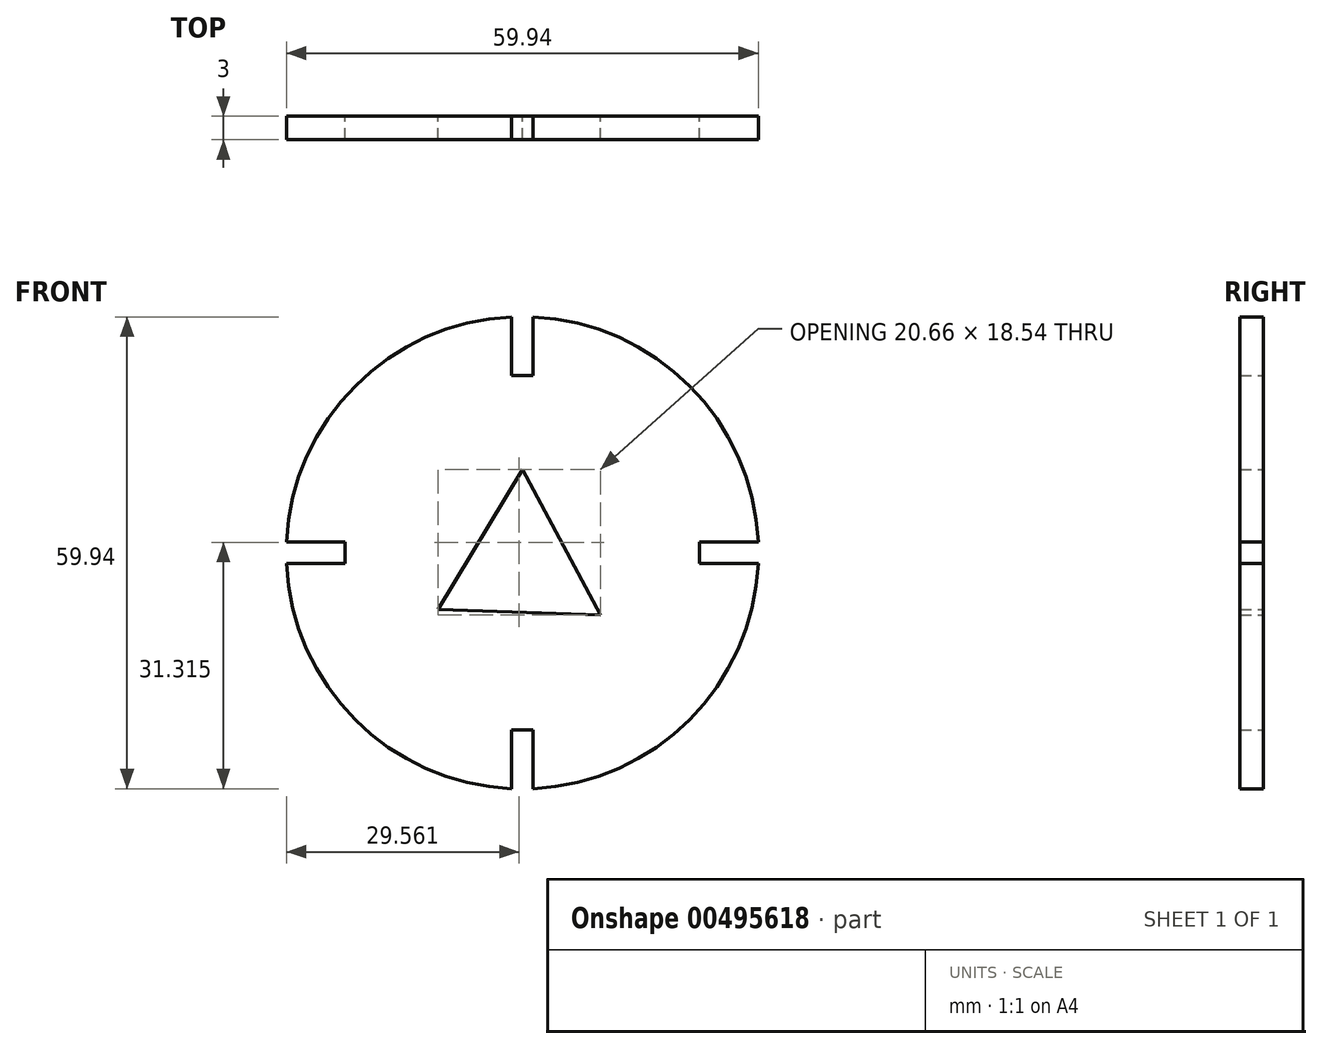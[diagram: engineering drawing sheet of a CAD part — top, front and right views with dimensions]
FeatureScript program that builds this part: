
annotation { "Feature Type Name" : "Feature", "Feature Type Description" : "" }
export const myFeature = defineFeature(function(context is Context, id is Id, definition is map)
    precondition{}
    {
        {
            var Q0;
            Q0=qCreatedBy(makeId("Front.planeOp"),FACE);
            var sketch = newSketch(context, id + "F0", { "sketchPlane" : qUnion([Q0])});
            skArc(sketch, "E0", {"start": v(-1.35, 29.97) * mm, "mid": v(-21.21, 21.21) * mm, "end": v(-29.97, 1.35) * mm});
            skLineSegment(sketch, "E1.bottom", {"start": v(1.35, 22.5) * mm, "end": v(-1.35, 22.5) * mm});
            skLineSegment(sketch, "E1.left", {"start": v(1.35, 22.5) * mm, "end": v(1.35, 29.97) * mm});
            skLineSegment(sketch, "E1.right", {"start": v(-1.35, 22.5) * mm, "end": v(-1.35, 29.97) * mm});
            skPoint(sketch, "E1.middle", {"position": v(0, 30) * mm});
            skLineSegment(sketch, "E2.1.0", {"start": v(-22.5, 1.35) * mm, "end": v(-29.97, 1.35) * mm});
            skLineSegment(sketch, "E2.1.1", {"start": v(-22.5, -1.35) * mm, "end": v(-29.97, -1.35) * mm});
            skLineSegment(sketch, "E2.1.2", {"start": v(-22.5, 1.35) * mm, "end": v(-22.5, -1.35) * mm});
            skLineSegment(sketch, "E2.2.0", {"start": v(-1.35, -22.5) * mm, "end": v(-1.35, -29.97) * mm});
            skLineSegment(sketch, "E2.2.1", {"start": v(1.35, -22.5) * mm, "end": v(1.35, -29.97) * mm});
            skLineSegment(sketch, "E2.2.2", {"start": v(-1.35, -22.5) * mm, "end": v(1.35, -22.5) * mm});
            skLineSegment(sketch, "E2.3.0", {"start": v(22.5, -1.35) * mm, "end": v(29.97, -1.35) * mm});
            skLineSegment(sketch, "E2.3.1", {"start": v(22.5, 1.35) * mm, "end": v(29.97, 1.35) * mm});
            skLineSegment(sketch, "E2.3.2", {"start": v(22.5, -1.35) * mm, "end": v(22.5, 1.35) * mm});
            skPoint(sketch, "E1.top.end.orphan", {"position": v(-1.35, 37.5) * mm});
            skPoint(sketch, "E3.orphan", {"position": v(1.35, 37.5) * mm});
            skPoint(sketch, "E4.orphan", {"position": v(37.5, 1.35) * mm});
            skPoint(sketch, "E5.orphan", {"position": v(37.5, -1.35) * mm});
            skArc(sketch, "E6.trimOffspring", {"start": v(29.97, 1.35) * mm, "mid": v(21.21, 21.21) * mm, "end": v(1.35, 29.97) * mm});
            skPoint(sketch, "E7.orphan", {"position": v(-37.5, 1.35) * mm});
            skPoint(sketch, "E8.orphan", {"position": v(-37.5, -1.35) * mm});
            skArc(sketch, "E9.trimOffspring", {"start": v(-29.97, -1.35) * mm, "mid": v(-21.21, -21.21) * mm, "end": v(-1.35, -29.97) * mm});
            skArc(sketch, "E10.trimOffspring", {"start": v(1.35, -29.97) * mm, "mid": v(21.21, -21.21) * mm, "end": v(29.97, -1.35) * mm});
            skPoint(sketch, "E11.orphan", {"position": v(1.35, -37.5) * mm});
            skPoint(sketch, "E12.orphan", {"position": v(-1.35, -37.5) * mm});
            skLineSegment(sketch, "E13", {"start": v(-10.74, -7.22) * mm, "end": v(0, 10.61) * mm});
            skLineSegment(sketch, "E14", {"start": v(0, 10.61) * mm, "end": v(9.92, -7.92) * mm});
            skLineSegment(sketch, "E15", {"start": v(9.92, -7.92) * mm, "end": v(-10.74, -7.22) * mm});
            skSolve(sketch);
        }
        {
            var Q0;
            Q0 = qSketchRegion(id + "F0", true);
            extrude(context, id + "F1", {"entities" : qUnion([Q0]), "depth" : 3 * mm, "offsetDistance" : 25 * mm});
        }
    });
